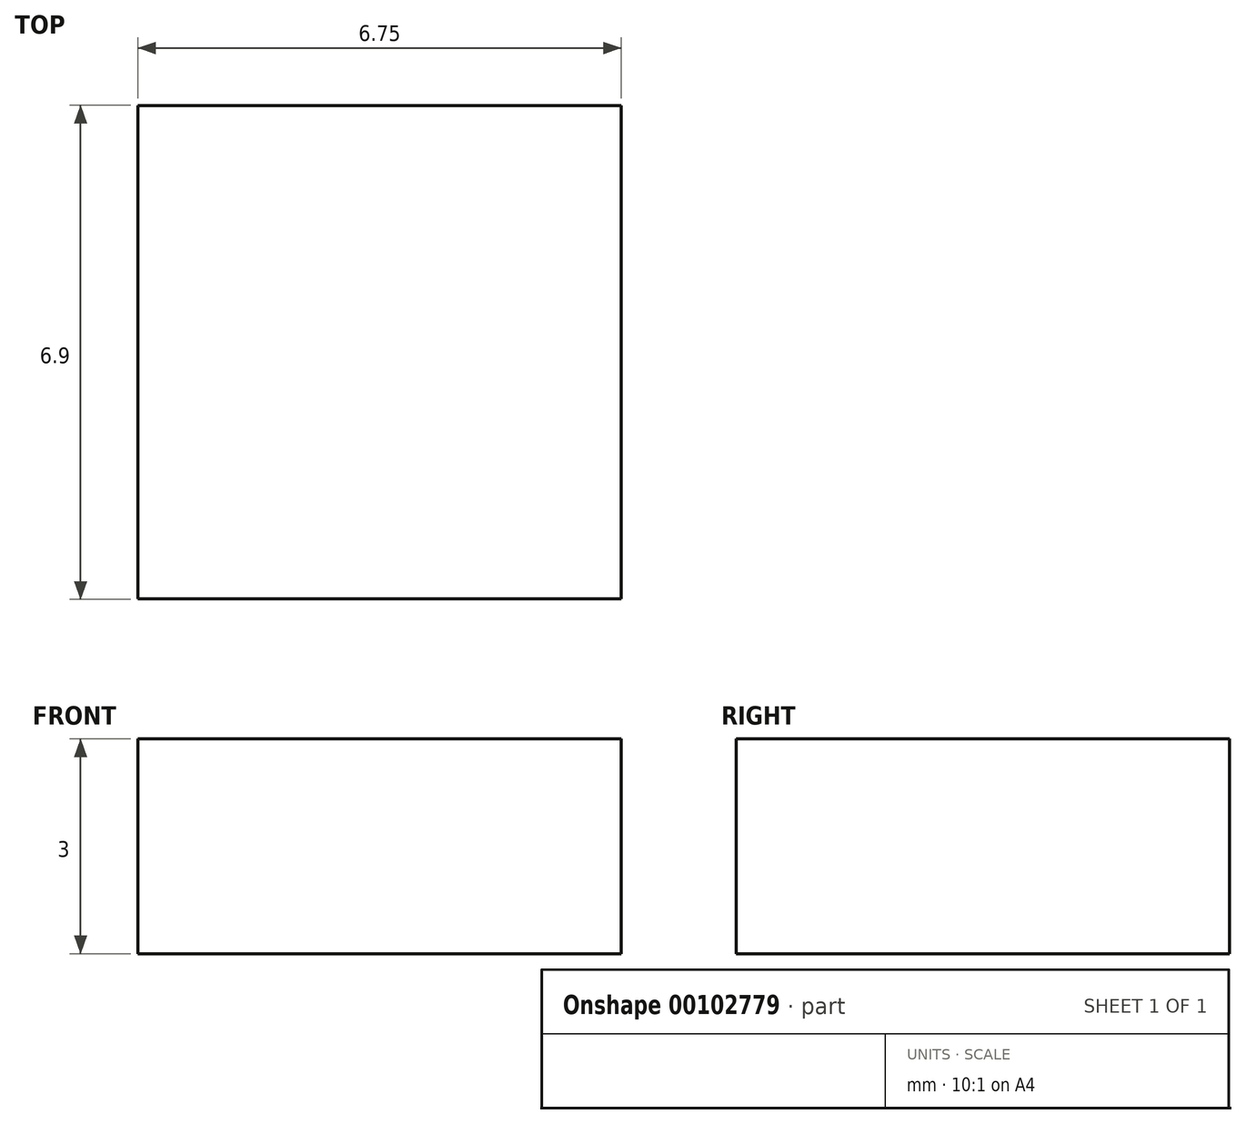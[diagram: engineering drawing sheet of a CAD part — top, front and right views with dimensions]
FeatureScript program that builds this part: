
annotation { "Feature Type Name" : "Feature", "Feature Type Description" : "" }
export const myFeature = defineFeature(function(context is Context, id is Id, definition is map)
    precondition{}
    {
        {
            var Q0;
            Q0=qCreatedBy(makeId("Top.planeOp"),FACE);
            var sketch = newSketch(context, id + "F0", { "sketchPlane" : qUnion([Q0])});
            skLineSegment(sketch, "E0", {"start": v(-10.2, 10.2) * mm, "end": v(10.2, -10.2) * mm, "construction": true});
            skSolve(sketch);
        }
        {
            var Q0;
            Q0=qCreatedBy(makeId("Top.planeOp"),FACE);
            var sketch = newSketch(context, id + "F1", { "sketchPlane" : qUnion([Q0])});
            skLineSegment(sketch, "E1.rect.bottom", {"start": v(10.2, 10.2) * mm, "end": v(-10.2, 10.2) * mm});
            skLineSegment(sketch, "E1.rect.top", {"start": v(10.2, -10.2) * mm, "end": v(-10.2, -10.2) * mm});
            skLineSegment(sketch, "E1.rect.left", {"start": v(10.2, 10.2) * mm, "end": v(10.2, -10.2) * mm});
            skLineSegment(sketch, "E1.rect.right", {"start": v(-10.2, 10.2) * mm, "end": v(-10.2, -10.2) * mm});
            skPoint(sketch, "E1.rect.middle", {"position": v(0, 0) * mm});
            skLineSegment(sketch, "E2", {"start": v(10.07, 10.2) * mm, "end": v(10.07, 5.43) * mm});
            skLineSegment(sketch, "E3", {"start": v(10.07, 5.43) * mm, "end": v(10.2, 5.34) * mm});
            skLineSegment(sketch, "E4", {"start": v(10.2, -5.34) * mm, "end": v(10.07, -5.43) * mm});
            skLineSegment(sketch, "E5", {"start": v(10.07, -5.43) * mm, "end": v(10.07, -10.2) * mm});
            skLineSegment(sketch, "E6", {"start": v(-7.86, -10.2) * mm, "end": v(-7.86, -5.59) * mm});
            skLineSegment(sketch, "E7", {"start": v(-7.86, -5.59) * mm, "end": v(-9.48, -4.45) * mm});
            skLineSegment(sketch, "E8", {"start": v(-9.48, -4.45) * mm, "end": v(-9.48, 4.45) * mm});
            skLineSegment(sketch, "E9", {"start": v(-9.48, 4.45) * mm, "end": v(-7.86, 5.59) * mm});
            skLineSegment(sketch, "E10", {"start": v(-7.86, 5.59) * mm, "end": v(-7.86, 10.2) * mm});
            skLineSegment(sketch, "E11.bottom", {"start": v(-10.2, 3.45) * mm, "end": v(-2.73, 3.45) * mm});
            skLineSegment(sketch, "E11.top", {"start": v(-10.2, -3.45) * mm, "end": v(-2.73, -3.45) * mm});
            skLineSegment(sketch, "E11.left", {"start": v(-10.2, 3.45) * mm, "end": v(-10.2, -3.45) * mm});
            skLineSegment(sketch, "E11.right", {"start": v(-2.73, 3.45) * mm, "end": v(-2.73, -3.45) * mm});
            skPoint(sketch, "E12.0", {"position": v(-10.2, 10.2) * mm});
            skPoint(sketch, "E13.0", {"position": v(10.2, -10.2) * mm});
            skLineSegment(sketch, "E14", {"start": v(10.2, 0) * mm, "end": v(-10.2, 0) * mm, "construction": true});
            skSolve(sketch);
        }
        {
            var Q0;
            {var subQ11=sQuery(id+"F1.wireOp",EDGE,"E2");Q0=makeQuery(id+"F1.imprint","IMPRINT",FACE,{"disambiguationData":[TD([[makeQuery(id+"F1.imprint","IMPRINT",EDGE,{"derivedFrom":subQ11}),-1.0]])]});}
            var Q1;
            {var subQ0=sQuery(id+"F1.wireOp",EDGE,"E11.right");Q1=makeQuery(id+"F1.imprint","IMPRINT",FACE,{"disambiguationData":[TD([[makeQuery(id+"F1.imprint","IMPRINT",EDGE,{"derivedFrom":subQ0}),-1.0]])]});}
            extrude(context, id + "F2", {"entities" : qUnion([Q0, Q1]), "depth" : 1.6 * mm});
        }
        {
            var Q0;
            {var subQ0=sQuery(id+"F1.wireOp",EDGE,"E11.left");Q0=makeQuery(id+"F1.imprint","IMPRINT",FACE,{"disambiguationData":[TD([[makeQuery(id+"F1.imprint","IMPRINT",EDGE,{"derivedFrom":subQ0}),1.0]])]});}
            var Q1;
            {var subQ0=sQuery(id+"F1.wireOp",EDGE,"E11.right");Q1=makeQuery(id+"F1.imprint","IMPRINT",FACE,{"disambiguationData":[TD([[makeQuery(id+"F1.imprint","IMPRINT",EDGE,{"derivedFrom":subQ0}),-1.0]])]});}
            extrude(context, id + "F3", {"entities" : qUnion([Q0, Q1]), "operationType" : NewBodyOperationType.ADD, "depth" : 3 * mm});
        }
    });
